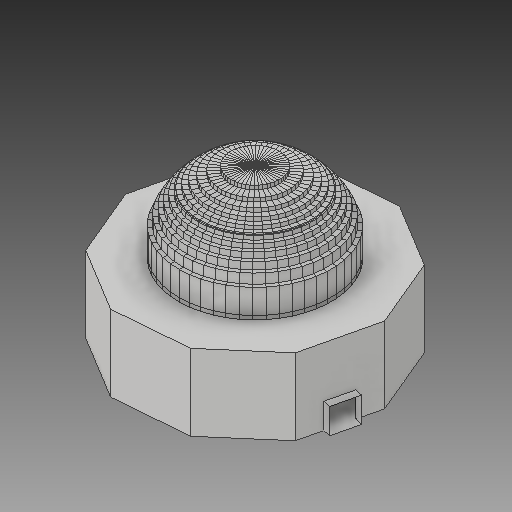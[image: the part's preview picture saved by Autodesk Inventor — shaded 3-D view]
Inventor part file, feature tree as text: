
AUTODESK INVENTOR PART (.ipt)
format: ipt  version: 2017 (Build 210142000, 142)  size: 2,411,008 bytes
history: native  units: in
note: dims shown in document units (in); Inventor stores cm internally (conversion verified against a paired STEP export)
features: extrude x8, sketch x7, other x3, plane x1, pattern_circular x1
ambient origin geometry x8: Origin, YZ Plane, XZ Plane, XY Plane, X Axis, Y Axis, Z Axis, Center Point
bodies: Solid1 (feature_tree)
feature tree (20):
  extrude  "bace"  Depth=1.0in TaperAngle=0.0deg
  extrude  "bace wall"  Depth=20.0in TaperAngle=0.0deg
  extrude  "bace ceiling"  Depth=1.0in
  other  "used to find the workplane for the dome"
  plane  "workplane for dome"
  extrude  "dome make"  Depth=1.0in TaperAngle=0.0deg
  sketch  "Sketch18"  dims[d190=45.0deg d192=1.0in d193=1.0in d194=1.0in d195=1.0in d196=1.0in d197=1.0in d198=1.0in d199=1.0in d200=0.0in d201=1.0in d202=0.0in d204=1.0in d205=19.685in d206=360.0deg d208=1.0in]
  extrude  "dome part cut 1"  Depth=2.5166in TaperAngle=90.0deg
  extrude  "dome part cut 2"  Depth=21.0in
  pattern_circular  "Circular Pattern6"  [2 undecoded]
  extrude  "door frame"  Depth=1.0in
  extrude  "corridor connection"  Depth=1.0in
  other  "Delete Faces of the room"
  other  "Delete Faces of dome"
  sketch  "Sketch1"  dims[d0=62.0in d1=1.0in d2=0.0in]
  sketch  "Sketch2"  dims[d4=1.0in d5=20.0in d6=0.0in]
  sketch  "Sketch3"  dims[d8=1.0in d9=0.0in d16=3.5in d17=6.6667in]
  sketch  "Sketch8"  dims[d18=1.0in d19=0.0in d107=1.0in d108=0.0in]
  sketch  "Sketch12"  dims[d109=40.0in d110=90.0deg d166=2.5166in]
  sketch  "Sketch17"  dims[d186=21.0in d187=0.0in d189=42.0in]
note: 2 required parameter values undecoded (feature->parameter linkage not recoverable at this tier; creation-order binding heuristic only, values carry confidence <= 0.55)
